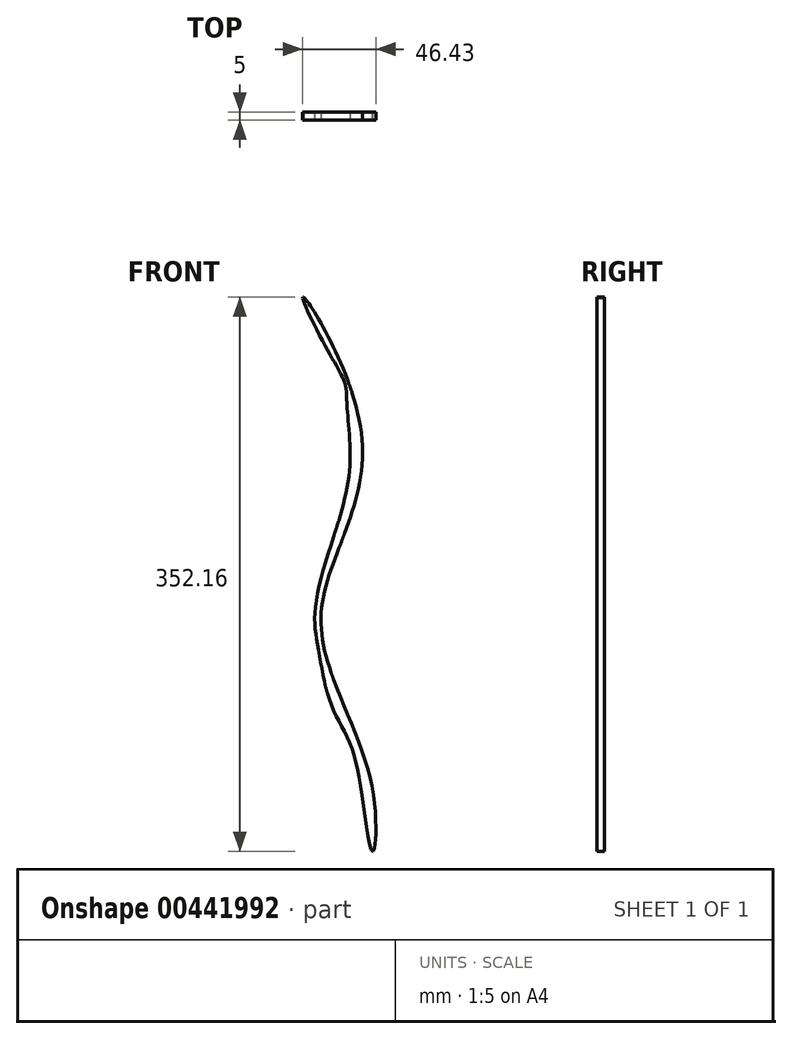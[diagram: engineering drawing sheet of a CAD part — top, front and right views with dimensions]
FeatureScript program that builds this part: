
annotation { "Feature Type Name" : "Feature", "Feature Type Description" : "" }
export const myFeature = defineFeature(function(context is Context, id is Id, definition is map)
    precondition{}
    {
        {
            var Q0;
            Q0=qCreatedBy(makeId("Front.planeOp"),FACE);
            var sketch = newSketch(context, id + "F0", { "sketchPlane" : qUnion([Q0])});
            skLineSegment(sketch, "E0", {"start": v(14.32, 410.31) * mm, "end": v(83.36, 477.03) * mm});
            skLineSegment(sketch, "E1", {"start": v(83.36, 477.03) * mm, "end": v(100.01, 0) * mm});
            skLineSegment(sketch, "E2", {"start": v(100.01, 0) * mm, "end": v(0, 0) * mm});
            skLineSegment(sketch, "E3", {"start": v(0, 0) * mm, "end": v(14.32, 410.31) * mm});
            skFitSpline(sketch, "E4", {"points": [v(37.19, 0) * mm, v(21.84, 67.95) * mm, v(41.19, 128.64) * mm, v(46.52, 182) * mm, v(28.51, 238.03) * mm, v(59.86, 330.75) * mm, v(61.86, 399.45) * mm, v(44.87, 439.83) * mm, v(52.53, 417.46) * mm, v(61.2, 381.44) * mm, v(59.86, 354.1) * mm, v(49.86, 318.74) * mm, v(35.85, 290.06) * mm, v(25.18, 260.04) * mm, v(22.51, 222.02) * mm, v(35.18, 193.34) * mm, v(42.52, 166) * mm, v(35.85, 129.98) * mm, v(19.84, 85.29) * mm, v(17.84, 53.94) * mm, v(37.19, 0) * mm]});
            skFitSpline(sketch, "E5", {"points": [v(12.29, 352.14) * mm, v(49.86, 262.71) * mm, v(23.85, 149.32) * mm, v(55.2, 45.93) * mm, v(56.53, 0) * mm, v(49.86, 35.26) * mm, v(42.52, 67.95) * mm, v(33.85, 85.29) * mm, v(26.82, 104.34) * mm, v(21.84, 130.64) * mm, v(19.84, 149.32) * mm, v(27.18, 185.34) * mm, v(41.85, 241.37) * mm, v(40.3, 283.6) * mm, v(39.2, 296.79) * mm, v(27.85, 318.74) * mm, v(12.29, 352.14) * mm]});
            skFitSpline(sketch, "E6", {"points": [v(35.85, 431.12) * mm, v(35.85, 375.44) * mm, v(73.87, 333.41) * mm, v(83.2, 282.72) * mm, v(69.2, 228.03) * mm, v(82.54, 143.98) * mm, v(79.87, 43.93) * mm, v(70.54, 0) * mm, v(78.54, 85.29) * mm, v(73.2, 157.32) * mm, v(59.86, 203.35) * mm, v(71.87, 273.38) * mm, v(72.54, 318.74) * mm, v(57.1, 341.1) * mm, v(35.85, 364.76) * mm, v(27.85, 380.77) * mm, v(35.85, 431.12) * mm]});
            skSolve(sketch);
        }
        {
            var Q0;
            Q0=makeQuery(id+"F0.imprint","IMPRINT",FACE,{"disambiguationData":[TD([[makeQuery(id+"F0.imprint","IMPRINT",EDGE,{"derivedFrom":sQuery(id+"F0.wireOp",EDGE,"E5")}),-1.0]])]});
            extrude(context, id + "F1", {"entities" : qUnion([Q0]), "depth" : 5 * mm});
        }
    });
